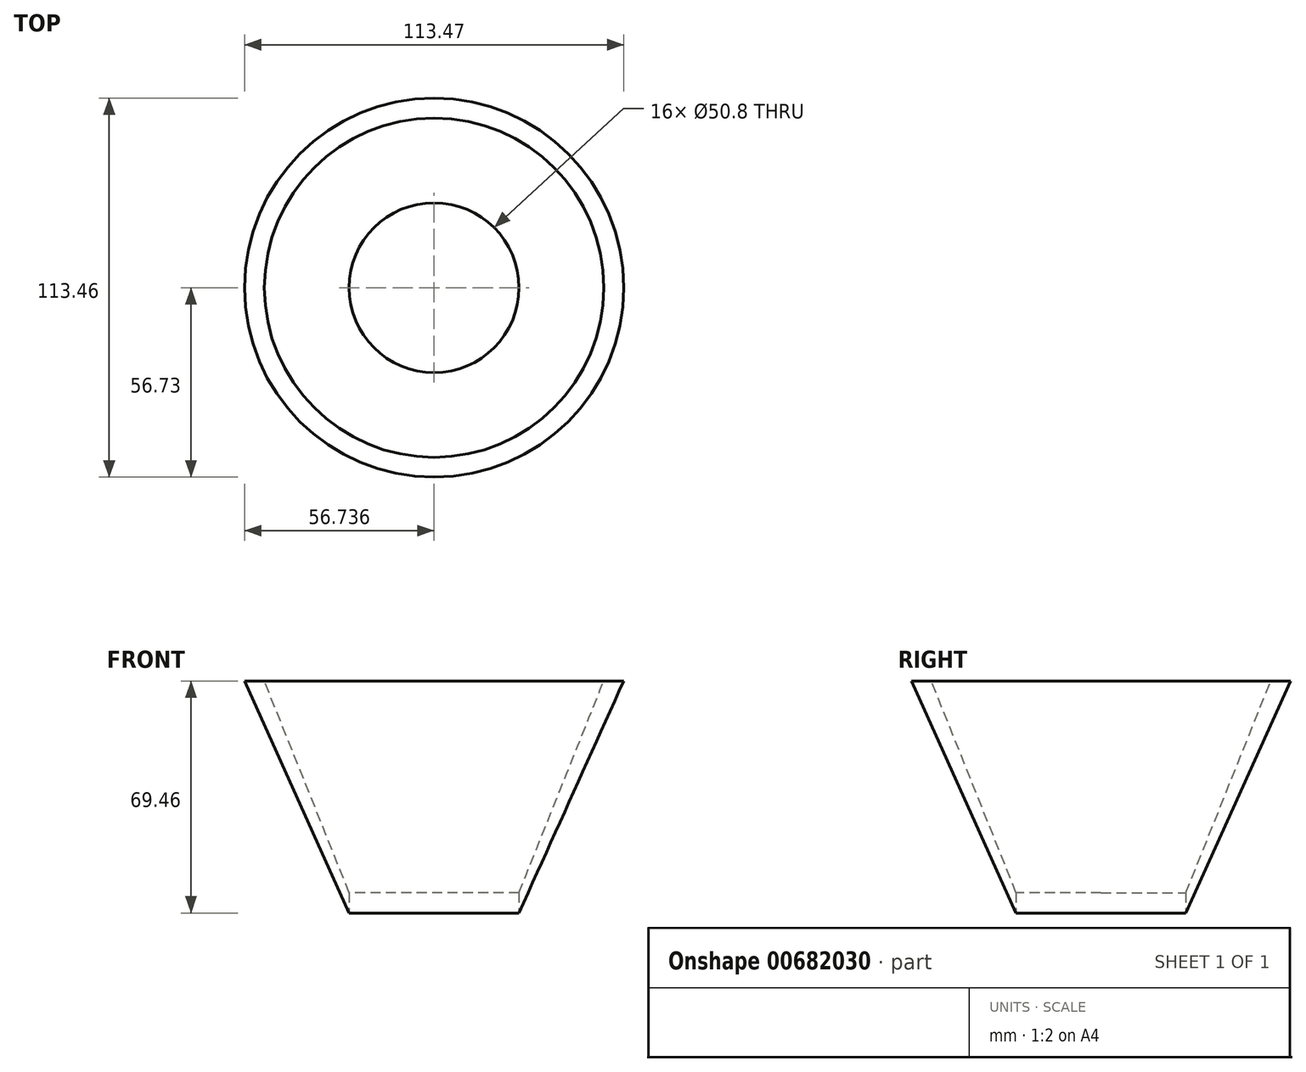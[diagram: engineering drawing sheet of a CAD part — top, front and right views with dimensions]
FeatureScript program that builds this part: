
annotation { "Feature Type Name" : "Feature", "Feature Type Description" : "" }
export const myFeature = defineFeature(function(context is Context, id is Id, definition is map)
    precondition{}
    {
        {
            var Q0;
            Q0=qCreatedBy(makeId("Front.planeOp"),FACE);
            var sketch = newSketch(context, id + "F0", { "sketchPlane" : qUnion([Q0])});
            skLineSegment(sketch, "E0", {"start": v(-39.95, -47.14) * mm, "end": v(-14.55, -47.14) * mm});
            skLineSegment(sketch, "E1", {"start": v(-14.55, -47.14) * mm, "end": v(16.78, 22.32) * mm});
            skLineSegment(sketch, "E2", {"start": v(16.78, 22.32) * mm, "end": v(10.82, 22.32) * mm});
            skLineSegment(sketch, "E3", {"start": v(10.82, 22.32) * mm, "end": v(-14.55, -41.07) * mm});
            skLineSegment(sketch, "E4", {"start": v(-14.55, -41.07) * mm, "end": v(-39.95, -41.07) * mm});
            skLineSegment(sketch, "E5", {"start": v(-39.95, -41.07) * mm, "end": v(-39.95, -47.14) * mm});
            skSolve(sketch);
        }
        {
            var Q0;
            Q0=makeQuery(id+"F0.imprint","IMPRINT",FACE,{"disambiguationData":[TD([[makeQuery(id+"F0.imprint","IMPRINT",EDGE,{"derivedFrom":sQuery(id+"F0.wireOp",EDGE,"E0")}),1.0]])]});
            var Q1;
            Q1=sQuery(id+"F0.wireOp",EDGE,"E5");
            revolve(context, id + "F1", {"entities" : qUnion([Q0]), "axis" : qUnion([Q1]), "revolveType" : RevolveType.FULL});
        }
        {
            var Q0;
            Q0=qCreatedBy(makeId("Top.planeOp"),FACE);
            var sketch = newSketch(context, id + "F2", { "sketchPlane" : qUnion([Q0])});
            skCircle(sketch, "E6", {"center": v(-40.69, 0) * mm, "radius": 24.7 * mm});
            skSolve(sketch);
        }
        {
            var Q0;
            Q0 = qSketchRegion(id + "F2", true);
            var Q1;
            Q1=makeQuery(id+"F1.opRevolve","SWEPT_FACE",FACE,{"disambiguationData":[OSD([sQuery(id+"F0.wireOp",EDGE,"E0")])]});
            extrude(context, id + "F3", {"entities" : qUnion([Q0, Q1]), "operationType" : NewBodyOperationType.REMOVE, "depth" : 50.8 * mm, "offsetDistance" : 25.4 * mm});
        }
    });
